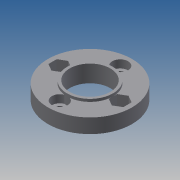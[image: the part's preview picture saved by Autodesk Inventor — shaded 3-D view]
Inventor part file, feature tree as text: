
AUTODESK INVENTOR PART (.ipt)
format: ipt  version: 2013 (Build 170138000, 138)  size: 144,384 bytes
history: native  units: mm
features: extrude x6, sketch x6, pattern_circular x2
ambient origin geometry x8: Origin, YZ Plane, XZ Plane, XY Plane, X Axis, Y Axis, Z Axis, Center Point
bodies: Solid1 (feature_tree)
feature tree (14):
  extrude  "Extrusion1"  Depth=4.5mm TaperAngle=0.0deg
  extrude  "Extrusion2"  Depth=1.0mm TaperAngle=0.0deg
  extrude  "Extrusion3"  Depth=1.0mm TaperAngle=0.0deg
  extrude  "Extrusion4"  Depth=3.5mm
  pattern_circular  "Circular Pattern1"  Count=4 Angle=360.0deg
  extrude  "Extrusion5"  Depth=3.0mm TaperAngle=0.0deg
  extrude  "Extrusion6"  Depth=5.5mm
  pattern_circular  "Circular Pattern2"  [2 undecoded]
  sketch  "Sketch1"  dims[d0=32.0mm d3=4.5mm d4=0.0mm]
  sketch  "Sketch2"  dims[d5=17.5mm d8=1.0mm d9=0.0mm]
  sketch  "Sketch3"  dims[d10=15.5mm d12=1.0mm d13=0.0mm]
  sketch  "Sketch4"  dims[d15=11.5mm d16=3.5mm]
  sketch  "Sketch5"  dims[d17=1.0mm d18=0.0mm d19=40.0mm d20=360.0deg]
  sketch  "Sketch6"  dims[d22=6.0mm d26=3.0mm d27=0.0mm d28=5.5mm d29=4.0mm d30=0.0mm d31=20.0mm d32=360.0deg]
note: 2 required parameter values undecoded (feature->parameter linkage not recoverable at this tier; creation-order binding heuristic only, values carry confidence <= 0.55)
